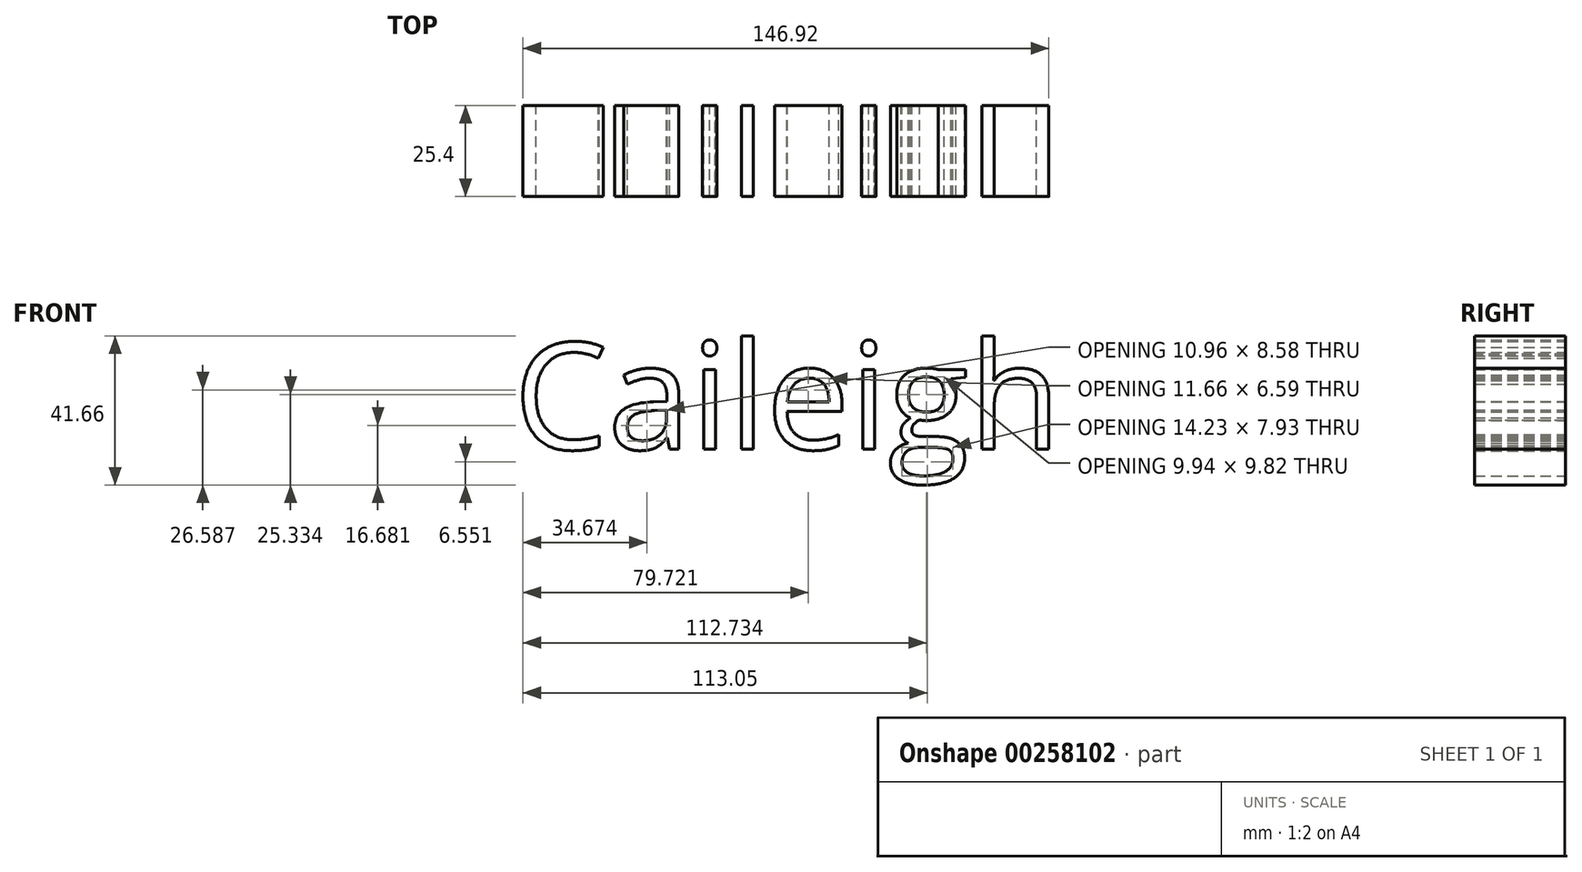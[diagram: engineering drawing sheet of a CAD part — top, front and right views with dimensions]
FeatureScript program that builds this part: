
annotation { "Feature Type Name" : "Feature", "Feature Type Description" : "" }
export const myFeature = defineFeature(function(context is Context, id is Id, definition is map)
    precondition{}
    {
        {
            var Q0;
            Q0=qCreatedBy(makeId("Front.planeOp"),FACE);
            var sketch = newSketch(context, id + "F0", { "sketchPlane" : qUnion([Q0])});
            skText(sketch, "E0", { "text": "Caileigh", "fontName": "OpenSans-Regular.ttf"});
            const initialGuessF0  = {"E0": [-0.07286, 0.02144, 1, 0, 0.02999]};
            skSetInitialGuess(sketch, initialGuessF0);
            skSolve(sketch);
        }
        {
            var Q0;
            Q0 = qSketchRegion(id + "F0", true);
            extrude(context, id + "F1", {"entities" : qUnion([Q0]), "depth" : 25.4 * mm});
        }
    });
